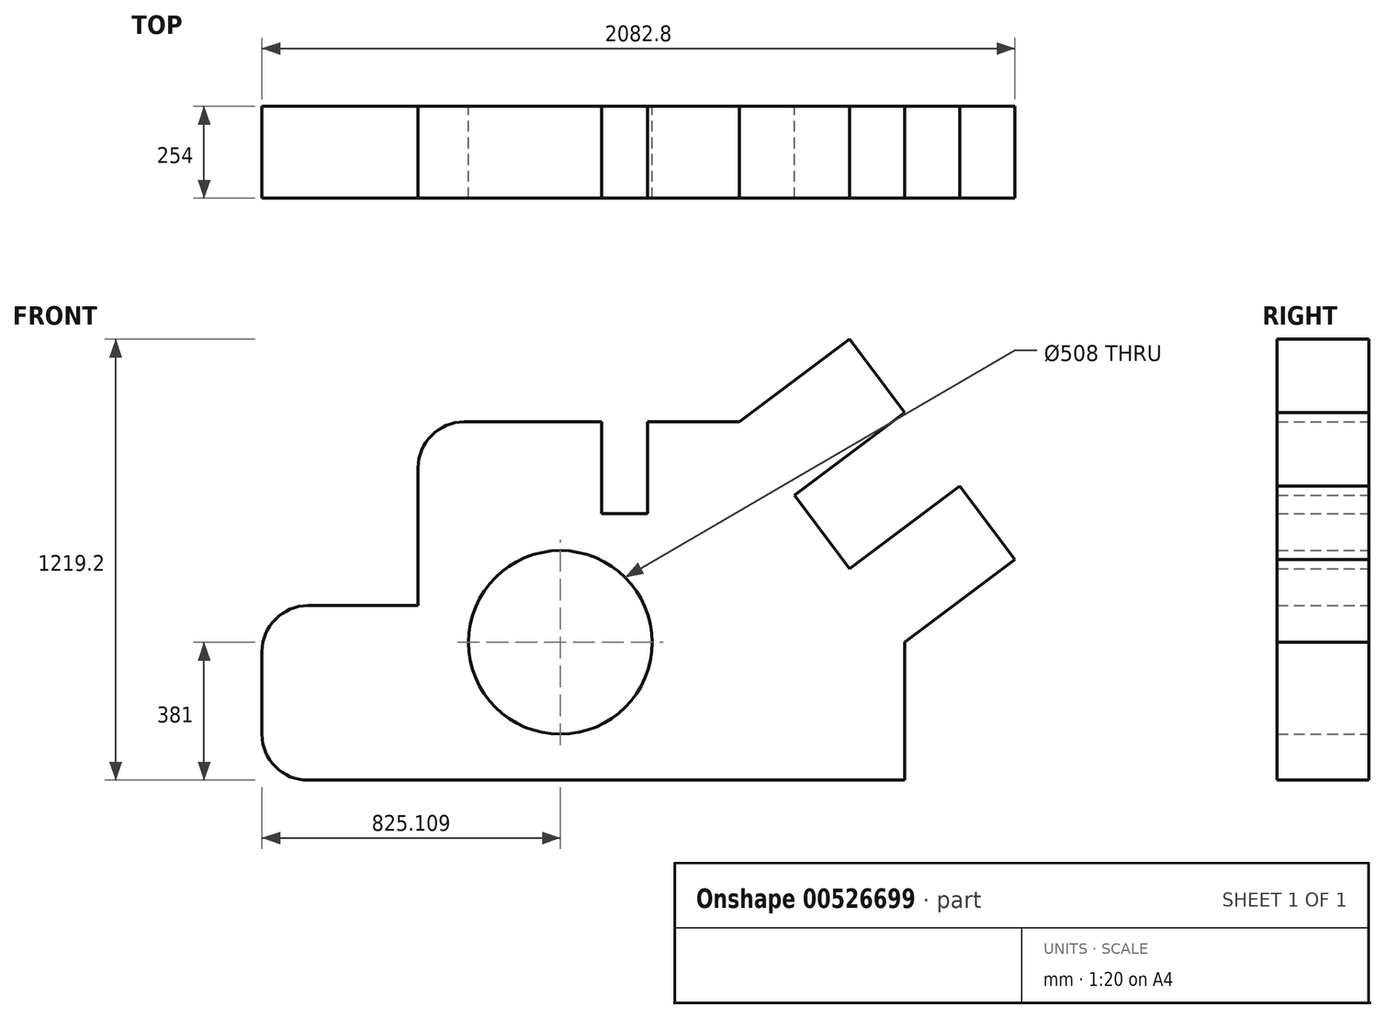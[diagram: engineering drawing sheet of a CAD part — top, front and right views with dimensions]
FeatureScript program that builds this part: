
annotation { "Feature Type Name" : "Feature", "Feature Type Description" : "" }
export const myFeature = defineFeature(function(context is Context, id is Id, definition is map)
    precondition{}
    {
        {
            var Q0;
            Q0=qCreatedBy(makeId("Front.planeOp"),FACE);
            var sketch = newSketch(context, id + "F0", { "sketchPlane" : qUnion([Q0])});
            skLineSegment(sketch, "E0", {"start": v(127, 0) * mm, "end": v(1778, 0) * mm});
            skLineSegment(sketch, "E1", {"start": v(1778, 0) * mm, "end": v(1778, 381) * mm});
            skLineSegment(sketch, "E2", {"start": v(0, 127) * mm, "end": v(0, 355.6) * mm});
            skPoint(sketch, "E3.visualSharp", {"position": v(0, 0) * mm});
            skArc(sketch, "E3.filletArc", {"start": v(0, 6.35) * mm, "mid": v(1.86, 1.86) * mm, "end": v(6.35, 0) * mm});
            skArc(sketch, "E4.filletArc", {"start": v(0, 12.7) * mm, "mid": v(3.72, 3.72) * mm, "end": v(12.7, 0) * mm});
            skLineSegment(sketch, "E5", {"start": v(1778, 381) * mm, "end": v(2082.8, 609.6) * mm});
            skLineSegment(sketch, "E6", {"start": v(2082.8, 609.6) * mm, "end": v(1930.4, 812.8) * mm});
            skLineSegment(sketch, "E7", {"start": v(1930.4, 812.8) * mm, "end": v(1625.6, 584.2) * mm});
            skLineSegment(sketch, "E8", {"start": v(1625.6, 584.2) * mm, "end": v(1473.2, 787.4) * mm});
            skLineSegment(sketch, "E9", {"start": v(1473.2, 787.4) * mm, "end": v(1778, 1016) * mm});
            skLineSegment(sketch, "E10", {"start": v(1778, 1016) * mm, "end": v(1625.6, 1219.2) * mm});
            skLineSegment(sketch, "E11", {"start": v(1625.6, 1219.2) * mm, "end": v(1320.8, 990.6) * mm});
            skLineSegment(sketch, "E12", {"start": v(1066.8, 990.6) * mm, "end": v(1066.8, 736.6) * mm});
            skLineSegment(sketch, "E13", {"start": v(1066.8, 736.6) * mm, "end": v(939.8, 736.6) * mm});
            skLineSegment(sketch, "E14", {"start": v(939.8, 736.6) * mm, "end": v(939.8, 990.6) * mm});
            skLineSegment(sketch, "E15", {"start": v(939.8, 990.6) * mm, "end": v(685.8, 990.6) * mm});
            skLineSegment(sketch, "E16", {"start": v(431.8, 736.6) * mm, "end": v(431.8, 482.6) * mm});
            skLineSegment(sketch, "E17", {"start": v(431.8, 482.6) * mm, "end": v(127, 482.6) * mm});
            skPoint(sketch, "E18.orphan", {"position": v(0, 508) * mm});
            skPoint(sketch, "E19.visualSharp", {"position": v(431.8, 990.6) * mm});
            skLineSegment(sketch, "E20", {"start": v(685.8, 990.6) * mm, "end": v(558.8, 990.6) * mm});
            skLineSegment(sketch, "E21", {"start": v(431.8, 736.6) * mm, "end": v(431.8, 863.6) * mm});
            skArc(sketch, "E22.filletArc", {"start": v(558.8, 990.6) * mm, "mid": v(469, 953.4) * mm, "end": v(431.8, 863.6) * mm});
            skPoint(sketch, "E23.visualSharp", {"position": v(0, 482.6) * mm});
            skArc(sketch, "E23.filletArc", {"start": v(127, 482.6) * mm, "mid": v(37.2, 445.4) * mm, "end": v(0, 355.6) * mm});
            skCircle(sketch, "E24", {"center": v(825.1, 381) * mm, "radius": 254 * mm});
            skArc(sketch, "E25.filletArc", {"start": v(0, 127) * mm, "mid": v(37.2, 37.2) * mm, "end": v(127, 0) * mm});
            skLineSegment(sketch, "E26", {"start": v(1066.8, 990.6) * mm, "end": v(1320.8, 990.6) * mm});
            skSolve(sketch);
        }
        {
            var Q0;
            Q0=makeQuery(id+"F0.imprint","IMPRINT",FACE,{"disambiguationData":[TD([[makeQuery(id+"F0.imprint","IMPRINT",EDGE,{"derivedFrom":sQuery(id+"F0.wireOp",EDGE,"E0")}),1.0]])]});
            extrude(context, id + "F1", {"entities" : qUnion([Q0]), "depth" : 254 * mm, "offsetDistance" : 25.4 * mm});
        }
    });
